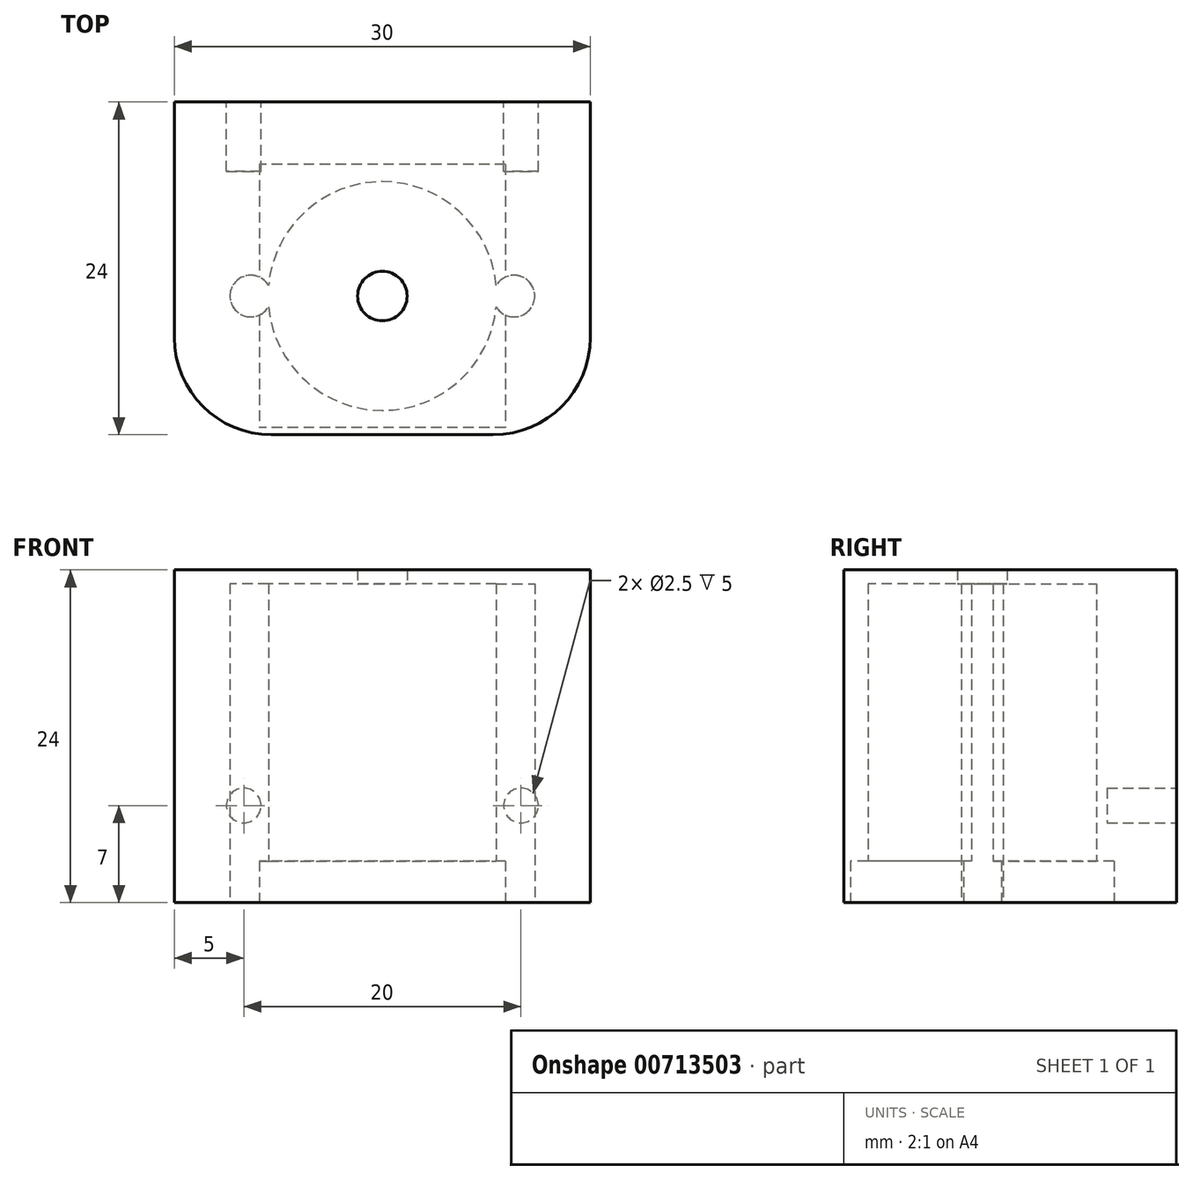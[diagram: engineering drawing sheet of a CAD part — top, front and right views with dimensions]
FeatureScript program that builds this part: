
annotation { "Feature Type Name" : "Feature", "Feature Type Description" : "" }
export const myFeature = defineFeature(function(context is Context, id is Id, definition is map)
    precondition{}
    {
        {
            var Q0;
            Q0=qCreatedBy(makeId("Top.planeOp"),FACE);
            var sketch = newSketch(context, id + "F0", { "sketchPlane" : qUnion([Q0])});
            skLineSegment(sketch, "E0.bottom", {"start": v(15, -10) * mm, "end": v(-15, -10) * mm});
            skLineSegment(sketch, "E0.top", {"start": v(15, 10) * mm, "end": v(-15, 10) * mm, "construction": true});
            skLineSegment(sketch, "E0.left", {"start": v(15, -10) * mm, "end": v(15, 10) * mm});
            skLineSegment(sketch, "E0.right", {"start": v(-15, -10) * mm, "end": v(-15, 10) * mm});
            skPoint(sketch, "E0.middle", {"position": v(0, 0) * mm});
            skLineSegment(sketch, "E1", {"start": v(0, 10.9) * mm, "end": v(0, -15.31) * mm, "construction": true});
            skLineSegment(sketch, "E2.bottom", {"start": v(15, 0) * mm, "end": v(-15, 0) * mm, "construction": true});
            skLineSegment(sketch, "E2.top", {"start": v(15, 14) * mm, "end": v(-15, 14) * mm});
            skLineSegment(sketch, "E2.left", {"start": v(15, 0) * mm, "end": v(15, 14) * mm});
            skLineSegment(sketch, "E2.right", {"start": v(-15, 0) * mm, "end": v(-15, 14) * mm});
            skSolve(sketch);
        }
        {
            var Q0;
            Q0=makeQuery(id+"F0.imprint","IMPRINT",FACE,{"disambiguationData":[TD([[makeQuery(id+"F0.imprint","IMPRINT",EDGE,{"derivedFrom":sQuery(id+"F0.wireOp",EDGE,"E0.bottom")}),-1.0]])]});
            extrude(context, id + "F1", {"entities" : qUnion([Q0]), "depth" : 24 * mm, "offsetDistance" : 25 * mm});
        }
        {
            var Q0;
            Q0=qCreatedBy(makeId("Top.planeOp"),FACE);
            var sketch = newSketch(context, id + "F2", { "sketchPlane" : qUnion([Q0])});
            skCircle(sketch, "E3", {"center": v(-9.5, 0) * mm, "radius": 1.5 * mm});
            skCircle(sketch, "E4", {"center": v(9.5, 0) * mm, "radius": 1.5 * mm});
            skLineSegment(sketch, "E5.bottom", {"start": v(15, -10) * mm, "end": v(-15, -10) * mm});
            skLineSegment(sketch, "E5.top", {"start": v(15, 10) * mm, "end": v(-15, 10) * mm, "construction": true});
            skLineSegment(sketch, "E5.left", {"start": v(15, -10) * mm, "end": v(15, 10) * mm});
            skLineSegment(sketch, "E5.right", {"start": v(-15, -10) * mm, "end": v(-15, 10) * mm});
            skPoint(sketch, "E5.middle", {"position": v(0, 0) * mm});
            skLineSegment(sketch, "E6", {"start": v(0, 10) * mm, "end": v(0, -18.37) * mm, "construction": true});
            skCircle(sketch, "E7", {"center": v(0, 0) * mm, "radius": 8.25 * mm});
            skLineSegment(sketch, "E8.bottom", {"start": v(15, 0) * mm, "end": v(-15, 0) * mm, "construction": true});
            skLineSegment(sketch, "E8.top", {"start": v(15, 21) * mm, "end": v(-15, 21) * mm});
            skLineSegment(sketch, "E8.left", {"start": v(15, 0) * mm, "end": v(15, 21) * mm});
            skLineSegment(sketch, "E8.right", {"start": v(-15, 0) * mm, "end": v(-15, 21) * mm});
            skSolve(sketch);
        }
        {
            var Q0;
            Q0=makeQuery(id+"F2.imprint","IMPRINT",FACE,{"disambiguationData":[TD([[makeQuery(id+"F2.imprint","IMPRINT",EDGE,{"derivedFrom":sQuery(id+"F2.wireOp",EDGE,"E7")}),1.0]])]});
            var Q1;
            Q1=makeQuery(id+"F2.imprint","IMPRINT",FACE,{"disambiguationData":[TD([[makeQuery(id+"F2.imprint","IMPRINT",EDGE,{"derivedFrom":sQuery(id+"F2.wireOp",EDGE,"E3")}),1.0]])]});
            var Q2;
            Q2=makeQuery(id+"F2.imprint","IMPRINT",FACE,{"disambiguationData":[TD([[makeQuery(id+"F2.imprint","IMPRINT",EDGE,{"derivedFrom":sQuery(id+"F2.wireOp",EDGE,"E4")}),1.0]])]});
            var Q3;
            Q3=sQuery(id+"F2.wireOp",EDGE,"E5.top");
            var Q4;
            Q4=sQuery(id+"F2.wireOp",EDGE,"E8.bottom");
            extrude(context, id + "F3", {"entities" : qUnion([Q0, Q1, Q2]), "operationType" : NewBodyOperationType.REMOVE, "surfaceEntities" : qUnion([Q3, Q4]), "depth" : 23 * mm, "offsetDistance" : 25 * mm});
        }
        {
            var Q0;
            Q0=makeQuery(id+"F3.boolean.opBoolean","COPY",FACE,{"derivedFrom":makeQuery(id+"F3.opExtrude","CAP_FACE",FACE,{"disambiguationData":[OSD([sQuery(id+"F2.wireOp",EDGE,"E7")])],"isStart":false})});
            var sketch = newSketch(context, id + "F4", { "sketchPlane" : qUnion([Q0])});
            skCircle(sketch, "E9", {"center": v(0, 0) * mm, "radius": 1.79 * mm});
            skSolve(sketch);
        }
        {
            var Q0;
            Q0=qSketchRegion(id+"F4",true);
            extrude(context, id + "F5", {"entities" : qUnion([Q0]), "operationType" : NewBodyOperationType.REMOVE, "oppositeDirection" : true, "depth" : 25 * mm, "offsetDistance" : 25 * mm});
        }
        {
            var Q0;
            Q0=makeQuery(id+"F1.opExtrude","CAP_FACE",FACE,{"disambiguationData":[OSD([sQuery(id+"F0.wireOp",EDGE,"E0.bottom"),sQuery(id+"F0.wireOp",EDGE,"E0.left"),sQuery(id+"F0.wireOp",EDGE,"E0.right"),sQuery(id+"F0.wireOp",EDGE,"E2.top"),sQuery(id+"F0.wireOp",EDGE,"E2.left"),sQuery(id+"F0.wireOp",EDGE,"E2.right")])],"isStart":true});
            var sketch = newSketch(context, id + "F6", { "sketchPlane" : qUnion([Q0])});
            skCircle(sketch, "E10", {"center": v(0, 0) * mm, "radius": 13 * mm});
            skLineSegment(sketch, "E11.bottom", {"start": v(8.87, -9.5) * mm, "end": v(-8.87, -9.5) * mm});
            skLineSegment(sketch, "E11.top", {"start": v(8.87, 9.5) * mm, "end": v(-8.87, 9.5) * mm});
            skLineSegment(sketch, "E11.left", {"start": v(8.87, -9.5) * mm, "end": v(8.87, 9.5) * mm});
            skLineSegment(sketch, "E11.right", {"start": v(-8.87, -9.5) * mm, "end": v(-8.87, 9.5) * mm});
            skSolve(sketch);
        }
        {
            var Q0;
            Q0=makeQuery(id+"F6.imprint","IMPRINT",FACE,{"disambiguationData":[TD([[makeQuery(id+"F6.imprint","IMPRINT",EDGE,{"derivedFrom":makeQuery(id+"F3.boolean.opBoolean","COPY",EDGE,{"derivedFrom":makeQuery(id+"F3.opExtrude","CAP_EDGE",EDGE,{"disambiguationData":[OSD([sQuery(id+"F2.wireOp",EDGE,"E7")])],"isStart":true})})}),-1.0]])]});
            var Q1;
            {var subQ0=sQuery(id+"F6.wireOp",EDGE,"E10");var subQ1=makeQuery(id+"F1.opExtrude","CAP_EDGE",EDGE,{"disambiguationData":[OSD([sQuery(id+"F0.wireOp",EDGE,"E0.bottom")])],"isStart":true});var subQ2=makeQuery(id+"F6.imprint","INTERSECT",VERTEX,{"disambiguationData":[OD(0.0)],"derivedFrom":[subQ1,subQ0]});Q1=makeQuery(id+"F6.imprint","IMPRINT",FACE,{"disambiguationData":[TD([[makeQuery(id+"F6.imprint","IMPRINT",EDGE,{"disambiguationData":[TD([[subQ2,-1.0]])],"derivedFrom":subQ0}),1.0]])]});}
            var Q2;
            {var subQ0=sQuery(id+"F6.wireOp",EDGE,"E11.left");var subQ4=makeQuery(id+"F3.boolean.opBoolean","COPY",EDGE,{"derivedFrom":makeQuery(id+"F3.opExtrude","CAP_EDGE",EDGE,{"disambiguationData":[OSD([sQuery(id+"F2.wireOp",EDGE,"E4")])],"isStart":true})});var subQ6=makeQuery(id+"F6.imprint","INTERSECT",VERTEX,{"disambiguationData":[OD(0.0)],"derivedFrom":[subQ4,subQ0]});Q2=makeQuery(id+"F6.imprint","IMPRINT",FACE,{"disambiguationData":[TD([[makeQuery(id+"F6.imprint","IMPRINT",EDGE,{"disambiguationData":[TD([[subQ6,1.0]])],"derivedFrom":subQ4}),1.0]])]});}
            var Q3;
            {var subQ5=sQuery(id+"F6.wireOp",EDGE,"E11.bottom");Q3=makeQuery(id+"F6.imprint","IMPRINT",FACE,{"disambiguationData":[TD([[makeQuery(id+"F6.imprint","IMPRINT",EDGE,{"derivedFrom":subQ5}),-1.0]])]});}
            var Q4;
            {var subQ0=sQuery(id+"F6.wireOp",EDGE,"E11.left");var subQ1=makeQuery(id+"F3.boolean.opBoolean","COPY",EDGE,{"derivedFrom":makeQuery(id+"F3.opExtrude","CAP_EDGE",EDGE,{"disambiguationData":[OSD([sQuery(id+"F2.wireOp",EDGE,"E4")])],"isStart":true})});var subQ2=makeQuery(id+"F6.imprint","INTERSECT",VERTEX,{"disambiguationData":[OD(0.0)],"derivedFrom":[subQ1,subQ0]});Q4=makeQuery(id+"F6.imprint","IMPRINT",FACE,{"disambiguationData":[TD([[makeQuery(id+"F6.imprint","IMPRINT",EDGE,{"disambiguationData":[TD([[subQ2,-1.0]])],"derivedFrom":subQ0}),-1.0]])]});}
            var Q5;
            {var subQ0=sQuery(id+"F6.wireOp",EDGE,"E11.left");var subQ1=makeQuery(id+"F3.boolean.opBoolean","COPY",EDGE,{"derivedFrom":makeQuery(id+"F3.opExtrude","CAP_EDGE",EDGE,{"disambiguationData":[OSD([sQuery(id+"F2.wireOp",EDGE,"E4")])],"isStart":true})});var subQ2=makeQuery(id+"F6.imprint","INTERSECT",VERTEX,{"disambiguationData":[OD(0.0)],"derivedFrom":[subQ1,subQ0]});Q5=makeQuery(id+"F6.imprint","IMPRINT",FACE,{"disambiguationData":[TD([[makeQuery(id+"F6.imprint","IMPRINT",EDGE,{"disambiguationData":[TD([[subQ2,-1.0]])],"derivedFrom":subQ0}),1.0]])]});}
            var Q6;
            {var subQ0=sQuery(id+"F6.wireOp",EDGE,"E11.right");var subQ1=makeQuery(id+"F3.boolean.opBoolean","COPY",EDGE,{"derivedFrom":makeQuery(id+"F3.opExtrude","CAP_EDGE",EDGE,{"disambiguationData":[OSD([sQuery(id+"F2.wireOp",EDGE,"E3")])],"isStart":true})});var subQ2=makeQuery(id+"F6.imprint","INTERSECT",VERTEX,{"disambiguationData":[OD(0.0)],"derivedFrom":[subQ1,subQ0]});Q6=makeQuery(id+"F6.imprint","IMPRINT",FACE,{"disambiguationData":[TD([[makeQuery(id+"F6.imprint","IMPRINT",EDGE,{"disambiguationData":[TD([[subQ2,-1.0]])],"derivedFrom":subQ0}),1.0]])]});}
            var Q7;
            {var subQ0=sQuery(id+"F6.wireOp",EDGE,"E11.right");var subQ1=makeQuery(id+"F3.boolean.opBoolean","COPY",EDGE,{"derivedFrom":makeQuery(id+"F3.opExtrude","CAP_EDGE",EDGE,{"disambiguationData":[OSD([sQuery(id+"F2.wireOp",EDGE,"E3")])],"isStart":true})});var subQ2=makeQuery(id+"F6.imprint","INTERSECT",VERTEX,{"disambiguationData":[OD(0.0)],"derivedFrom":[subQ1,subQ0]});Q7=makeQuery(id+"F6.imprint","IMPRINT",FACE,{"disambiguationData":[TD([[makeQuery(id+"F6.imprint","IMPRINT",EDGE,{"disambiguationData":[TD([[subQ2,-1.0]])],"derivedFrom":subQ0}),-1.0]])]});}
            var Q8;
            {var subQ0=sQuery(id+"F6.wireOp",EDGE,"E11.right");var subQ4=makeQuery(id+"F3.boolean.opBoolean","COPY",EDGE,{"derivedFrom":makeQuery(id+"F3.opExtrude","CAP_EDGE",EDGE,{"disambiguationData":[OSD([sQuery(id+"F2.wireOp",EDGE,"E3")])],"isStart":true})});var subQ6=makeQuery(id+"F6.imprint","INTERSECT",VERTEX,{"disambiguationData":[OD(0.0)],"derivedFrom":[subQ4,subQ0]});Q8=makeQuery(id+"F6.imprint","IMPRINT",FACE,{"disambiguationData":[TD([[makeQuery(id+"F6.imprint","IMPRINT",EDGE,{"disambiguationData":[TD([[subQ6,-1.0]])],"derivedFrom":subQ4}),1.0]])]});}
            var Q9;
            {var subQ4=sQuery(id+"F6.wireOp",EDGE,"E11.top");Q9=makeQuery(id+"F6.imprint","IMPRINT",FACE,{"disambiguationData":[TD([[makeQuery(id+"F6.imprint","IMPRINT",EDGE,{"derivedFrom":subQ4}),1.0]])]});}
            extrude(context, id + "F7", {"entities" : qUnion([Q0, Q1, Q2, Q3, Q4, Q5, Q6, Q7, Q8, Q9]), "operationType" : NewBodyOperationType.REMOVE, "oppositeDirection" : true, "depth" : 3 * mm, "offsetDistance" : 25 * mm});
        }
        {
            var Q0;
            Q0=makeQuery(id+"F1.opExtrude","SWEPT_FACE",FACE,{"disambiguationData":[OSD([sQuery(id+"F0.wireOp",EDGE,"E2.top")])]});
            var sketch = newSketch(context, id + "F8", { "sketchPlane" : qUnion([Q0])});
            skCircle(sketch, "E12", {"center": v(-10, 7) * mm, "radius": 1.25 * mm});
            skLineSegment(sketch, "E13", {"start": v(-10, 24) * mm, "end": v(-10, 0) * mm, "construction": true});
            skCircle(sketch, "E14.MirrorC", {"center": v(10, 7) * mm, "radius": 1.25 * mm});
            skSolve(sketch);
        }
        {
            var Q0;
            Q0=qSketchRegion(id+"F8",true);
            extrude(context, id + "F9", {"entities" : qUnion([Q0]), "operationType" : NewBodyOperationType.REMOVE, "oppositeDirection" : true, "depth" : 5 * mm, "offsetDistance" : 25 * mm});
        }
        {
            var Q0;
            Q0=makeQuery(id+"F1.opExtrude","SWEPT_EDGE",EDGE,{"disambiguationData":[OSD([sQuery(id+"F0.wireOp",EDGE,"E0.bottom"),sQuery(id+"F0.wireOp",EDGE,"E0.right")])]});
            var Q1;
            Q1=makeQuery(id+"F1.opExtrude","SWEPT_EDGE",EDGE,{"disambiguationData":[OSD([sQuery(id+"F0.wireOp",EDGE,"E0.bottom"),sQuery(id+"F0.wireOp",EDGE,"E0.left")])]});
            fillet(context, id + "F10", {"entities" : qUnion([Q0, Q1]), "radius" : 7 * mm, "tangentPropagation" : true, "allowEdgeOverflow" : false});
        }
    });
